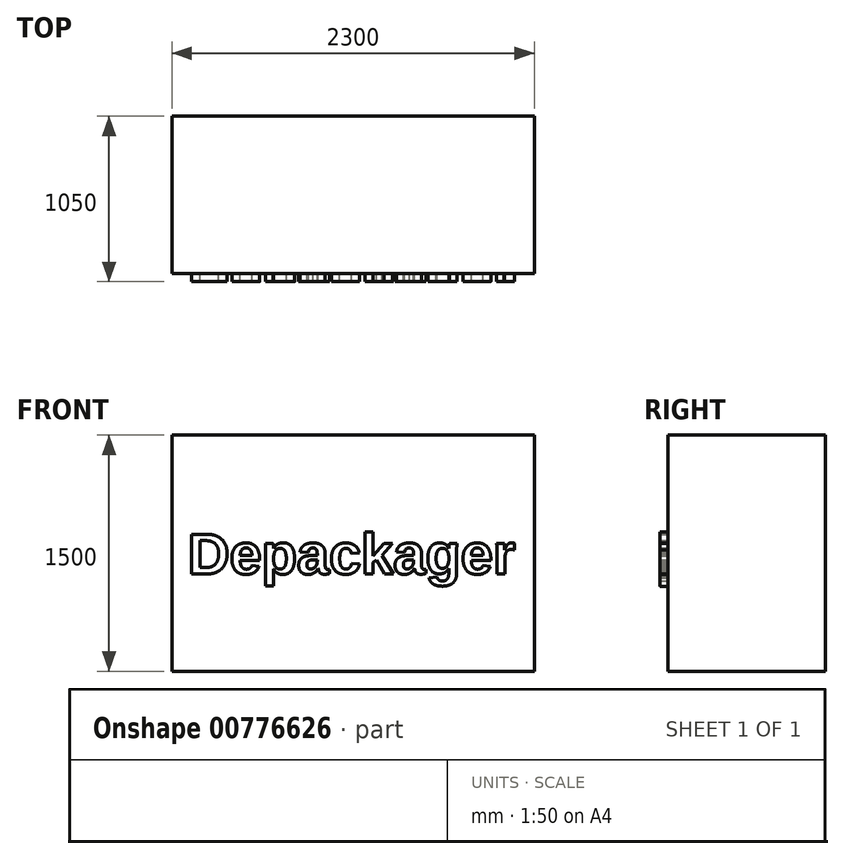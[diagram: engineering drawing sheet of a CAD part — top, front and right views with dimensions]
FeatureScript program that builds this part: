
annotation { "Feature Type Name" : "Feature", "Feature Type Description" : "" }
export const myFeature = defineFeature(function(context is Context, id is Id, definition is map)
    precondition{}
    {
        {
            var Q0;
            Q0=qCreatedBy(makeId("Front.planeOp"),FACE);
            var sketch = newSketch(context, id + "F0", { "sketchPlane" : qUnion([Q0])});
            skLineSegment(sketch, "E0.bottom", {"start": v(-1150, 750) * mm, "end": v(1150, 750) * mm});
            skLineSegment(sketch, "E0.top", {"start": v(-1150, -750) * mm, "end": v(1150, -750) * mm});
            skLineSegment(sketch, "E0.left", {"start": v(-1150, 750) * mm, "end": v(-1150, -750) * mm});
            skLineSegment(sketch, "E0.right", {"start": v(1150, 750) * mm, "end": v(1150, -750) * mm});
            skPoint(sketch, "E0.middle", {"position": v(0, 0) * mm});
            skSolve(sketch);
        }
        {
            var Q0;
            Q0 = qSketchRegion(id + "F0", true);
            extrude(context, id + "F1", {"entities" : qUnion([Q0]), "oppositeDirection" : true, "depth" : 1000 * mm, "offsetDistance" : 25 * mm});
        }
        {
            var Q0;
            Q0=makeQuery(id+"F1.opExtrude","CAP_FACE",FACE,{"disambiguationData":[OSD([sQuery(id+"F0.wireOp",EDGE,"E0.bottom"),sQuery(id+"F0.wireOp",EDGE,"E0.top"),sQuery(id+"F0.wireOp",EDGE,"E0.left"),sQuery(id+"F0.wireOp",EDGE,"E0.right")])],"isStart":true});
            var sketch = newSketch(context, id + "F2", { "sketchPlane" : qUnion([Q0])});
            skText(sketch, "E1", { "text": "Depackager", "fontName": "Arimo-Bold.ttf"});
            skPoint(sketch, "E2", {"position": v(0, 0) * mm});
            const initialGuessF2  = {"E1": [-1.05, -0.13208, 1, 0, 0.26416]};
            skSetInitialGuess(sketch, initialGuessF2);
            skSolve(sketch);
        }
        {
            var Q0;
            Q0 = qSketchRegion(id + "F2", true);
            extrude(context, id + "F3", {"entities" : qUnion([Q0]), "operationType" : NewBodyOperationType.ADD, "depth" : 50 * mm, "offsetDistance" : 25 * mm});
        }
    });
